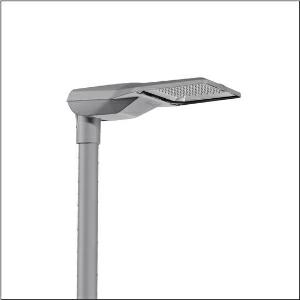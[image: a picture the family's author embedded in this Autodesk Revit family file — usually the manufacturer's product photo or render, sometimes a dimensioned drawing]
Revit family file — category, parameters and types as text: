
# Revit family: streetlight_sl_21_iq_midi___st1_5a_5xe3p31d08mb_51c0
name_source: partatom
category: Lighting Fixtures
units: mm (PartAtom-declared; Revit-internal decimal feet)

## family parameters
Cut with Voids When Loaded = No
Host = Face
Light Source = No
Part Type = Normal
Room Calculation Point = No
Round Connector Dimension = Use Diameter
Shared = No

## types (1)
- --- (1 x LED, 19170 lm, 146.7 W, 3000K)
    Apparent Load = 147 VA
    CIE Flux Codes = 22 53 95 100 100
    Color Rendering = 70
    Color Temperature = 3000K
    Default Elevation = 1800 mm
    Description = Streetlight SL 21 iQ midi, mast luminaire, primary light control with lens, of PMMA, primary optical cover: cover, of toughened safety glass, transparent, light distribution: ST1.5a, light emission: direct distribution, primary light characteristic: asymmetric, installation type: post-top, side-entry, LED, High Power LED, rated luminous flux: 19.170lm, luminous efficacy: 131lm/W, light colour: 730, colour temperature: 3000K, control: Auto-Match, Temp-Guard, Lumen-Switch, Night-Set, Smart-Wire, Light-Fading, Desk-Remote (wireless, voltage-free reading and setting of iQ features in the workshop via application-optimized NFC function/RFID function), optimised constant luminous flux control (CLO 2.0), presetting dimming linear, mains connection: 230..240V, AC, 50/60Hz, start of lifetime: 147W, end of service life: 161W, reduction: 62W, luminaire housing, of diecast aluminium, powder-coated, Siteco® metallic grey (DB 702S), corrosivity category C5 mid according to DIN EN ISO 12944, please order mast flange separately, inclination adjustable: 0°, 5°, 10°, 15°, sealing non-destructively replaceable, multi-level sealing system, length: 644mm, width: 335mm, height: 110mm, mast flange for spigot size: 42mm (side-entry): 5XC10008XM4, 60/48mm (side-entry/post-top): 5XC10108XM2, 76/60mm (side-entry/post-top): 5XC10108XM1, protection rating (complete): IP66, insulation class (complete): insulation class II (safety insulation), certification: CE, ENEC, ENEC+, VDE, impact resistance: IK09, permissible operating ambient temperature for outdoor applications: -40..+50°C, standard-compliant lighting for roads and squares, packaging unit: 1 piece

Light Distribution: ST1.5a
    Height = 111 mm
    Lamp = 1 x LED
    Lamp Light Flux = 19170 lm
    Lamp Power = 146.7 W
    Lamp count = 1
    Length = 644 mm
    Luminous efficacy = 131 lm/W
    Manufacturer = Siteco
    ModVariant = No
    Model = 5XE3P31D08MB
    Number of Poles = 1
    OnlyDefault = Yes
    Power Factor = 1
    Product Name = Streetlight SL 21 iQ midi | ST1.5a
    Product group = mast luminaire | pylon top
    ProductGroupID = 6100
    Protection Class = Protection class II
    Protection Degree = IP 66
    RLX_Detail_Level = 1
    RLX_Emergency_Light_Flux = 0 lm
    RLX_Emergency_Type = 0
    RLX_Emergency_Type_DB = No
    RlxData = <blob elided: 94201 chars, md5=45aed08b>
    Socket = socket
    Standby Power = 0 W
    System Light Flux = 19169 lm
    System Power = 147 W
    Type Comments = factory setting: luminous flux: 100 % | dim-lin: 254 | 753 mA
    Type Image = l_1004298.jpg
    URL = http://relux.com
    VarID = @adj_127489
    Voltage = 0 V
    Weight = 0.00 kg
    Width = 336 mm

## geometry (parser evidence)
native form markers: Blend x4, Sweep x12
no freeform markers — native parametric forms only
